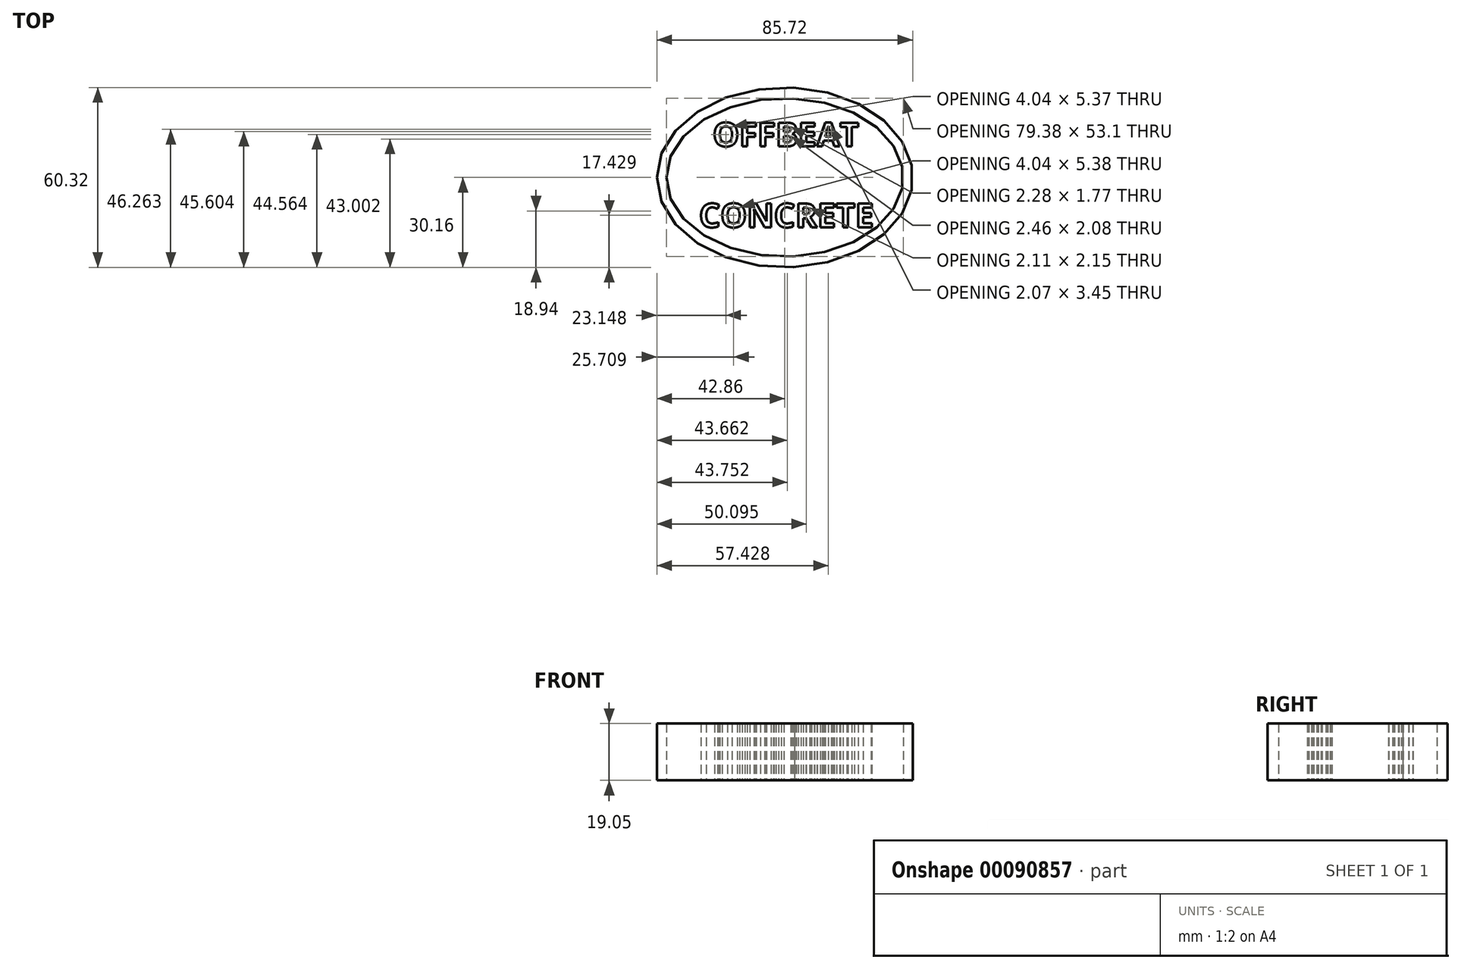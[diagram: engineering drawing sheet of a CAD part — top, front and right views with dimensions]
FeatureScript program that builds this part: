
annotation { "Feature Type Name" : "Feature", "Feature Type Description" : "" }
export const myFeature = defineFeature(function(context is Context, id is Id, definition is map)
    precondition{}
    {
        {
            var Q0;
            Q0=qCreatedBy(makeId("Top.planeOp"),FACE);
            var sketch = newSketch(context, id + "F0", { "sketchPlane" : qUnion([Q0])});
            skEllipse(sketch, "E0", {"center": v(0, 0) * mm, "majorRadius": 30.16 * mm, "minorRadius": 42.86 * mm, "majorAxis": v(0, 1)});
            skEllipse(sketch, "E1", {"center": v(0, 0) * mm, "majorRadius": 26.55 * mm, "minorRadius": 39.69 * mm, "majorAxis": v(0, 1)});
            skSolve(sketch);
        }
        {
            var Q0;
            Q0=qCreatedBy(makeId("Top.planeOp"),FACE);
            var sketch = newSketch(context, id + "F1", { "sketchPlane" : qUnion([Q0])});
            skText(sketch, "E2", { "text": "OFFBEAT", "fontName": "OpenSans-Bold.ttf"});
            skText(sketch, "E3", { "text": "CONCRETE", "fontName": "OpenSans-Bold.ttf"});
            const initialGuessF1  = {"E2": [-0.02415, 0.01041, 1, 0, 0.00803], "E3": [-0.02871, -0.01673, 1, 0, 0.00804]};
            skSetInitialGuess(sketch, initialGuessF1);
            skSolve(sketch);
        }
        {
            var Q0;
            Q0=qCreatedBy(makeId("Top.planeOp"),FACE);
            var sketch = newSketch(context, id + "F2", { "sketchPlane" : qUnion([Q0])});
            skSolve(sketch);
        }
        {
            var Q0;
            Q0 = qSketchRegion(id + "F2", true);
            var Q1;
            Q1=makeQuery(id+"F0.imprint","IMPRINT",FACE,{"disambiguationData":[TD([[makeQuery(id+"F0.imprint","IMPRINT",EDGE,{"derivedFrom":sQuery(id+"F0.wireOp",EDGE,"E0")}),1.0]])]});
            extrude(context, id + "F3", {"entities" : qUnion([Q0, Q1]), "depth" : 19.05 * mm});
        }
        {
            var Q0;
            Q0 = qSketchRegion(id + "F1", true);
            extrude(context, id + "F4", {"entities" : qUnion([Q0]), "depth" : 19.05 * mm});
        }
    });
